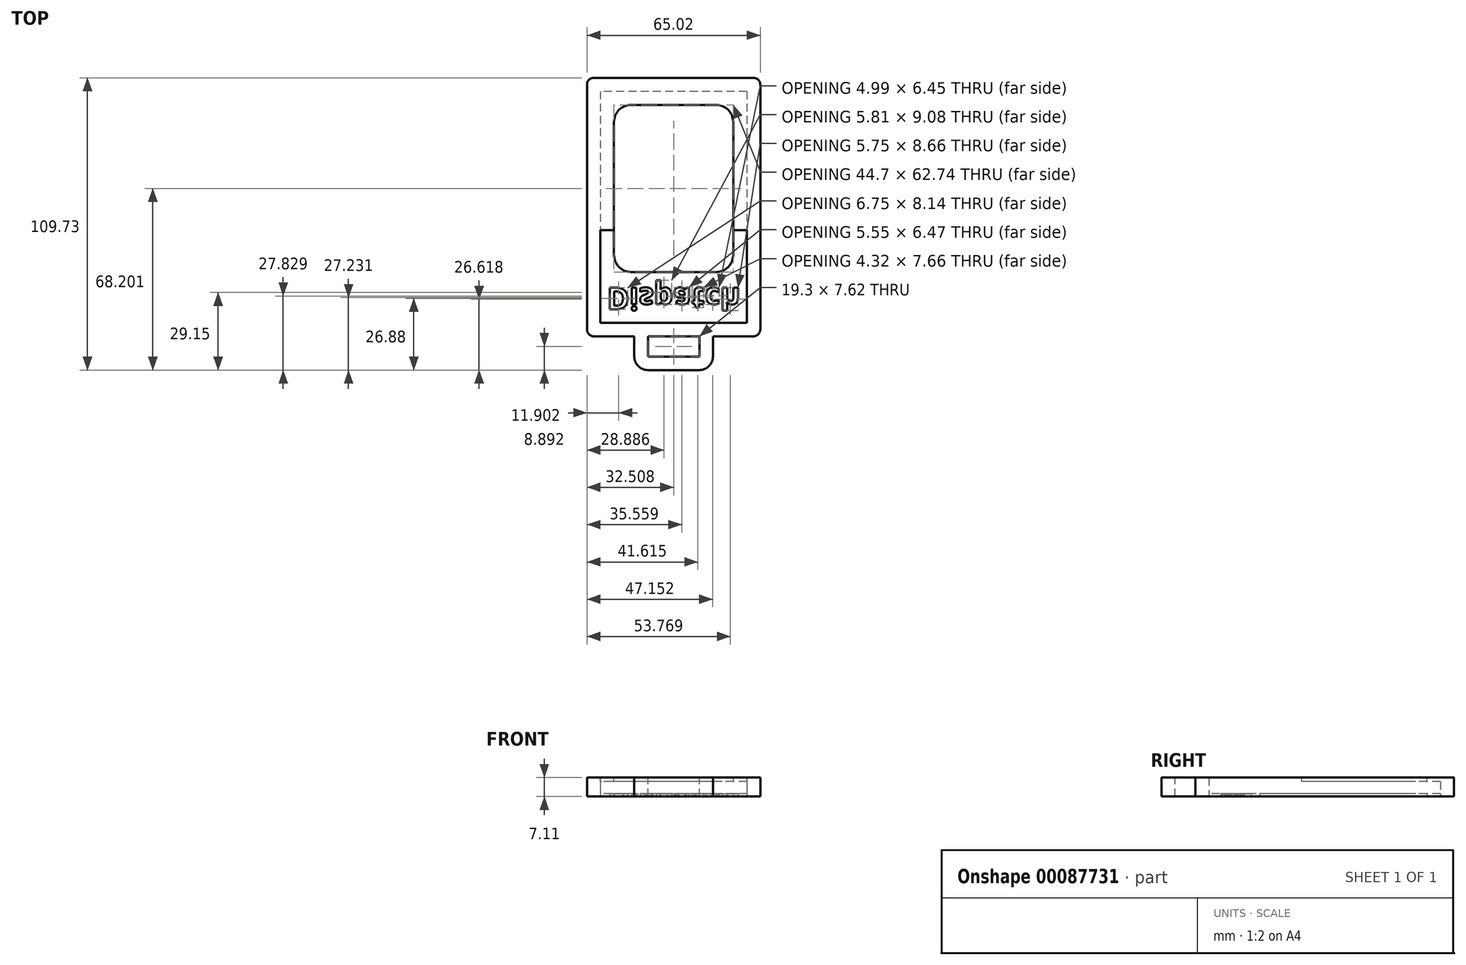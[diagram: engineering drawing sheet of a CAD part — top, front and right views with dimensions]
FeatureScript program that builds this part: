
annotation { "Feature Type Name" : "Feature", "Feature Type Description" : "" }
export const myFeature = defineFeature(function(context is Context, id is Id, definition is map)
    precondition{}
    {
        {
            var Q0;
            Q0=qCreatedBy(makeId("Top.planeOp"),FACE);
            var sketch = newSketch(context, id + "F0", { "sketchPlane" : qUnion([Q0])});
            skLineSegment(sketch, "E0.bottom", {"start": v(0, 0) * mm, "end": v(-54.86, 0) * mm});
            skLineSegment(sketch, "E0.top", {"start": v(0, -86.87) * mm, "end": v(-54.86, -86.87) * mm});
            skLineSegment(sketch, "E0.left", {"start": v(0, 0) * mm, "end": v(0, -86.87) * mm});
            skLineSegment(sketch, "E0.right", {"start": v(-54.86, 0) * mm, "end": v(-54.86, -86.87) * mm});
            skLineSegment(sketch, "E1.bottom", {"start": v(-59.94, 5.08) * mm, "end": v(5.08, 5.08) * mm});
            skLineSegment(sketch, "E1.top", {"start": v(-59.94, -91.95) * mm, "end": v(5.08, -91.95) * mm});
            skLineSegment(sketch, "E1.left", {"start": v(-59.94, 5.08) * mm, "end": v(-59.94, -91.95) * mm});
            skLineSegment(sketch, "E1.right", {"start": v(5.08, 5.08) * mm, "end": v(5.08, -91.95) * mm});
            skSolve(sketch);
        }
        {
            var Q0;
            Q0 = qSketchRegion(id + "F0", true);
            extrude(context, id + "F1", {"entities" : qUnion([Q0]), "depth" : 7.11 * mm});
        }
        {
            var Q0;
            Q0=makeQuery(id+"F1.opExtrude","CAP_FACE",FACE,{"disambiguationData":[OSD([sQuery(id+"F0.wireOp",EDGE,"E0.bottom"),sQuery(id+"F0.wireOp",EDGE,"E0.top"),sQuery(id+"F0.wireOp",EDGE,"E0.left"),sQuery(id+"F0.wireOp",EDGE,"E0.right"),sQuery(id+"F0.wireOp",EDGE,"E1.bottom"),sQuery(id+"F0.wireOp",EDGE,"E1.top"),sQuery(id+"F0.wireOp",EDGE,"E1.left"),sQuery(id+"F0.wireOp",EDGE,"E1.right")])],"isStart":true});
            var sketch = newSketch(context, id + "F2", { "sketchPlane" : qUnion([Q0])});
            skLineSegment(sketch, "E2.bottom", {"start": v(-54.86, 0) * mm, "end": v(0, 0) * mm});
            skLineSegment(sketch, "E2.top", {"start": v(-54.86, 86.87) * mm, "end": v(0, 86.87) * mm});
            skLineSegment(sketch, "E2.left", {"start": v(-54.86, 0) * mm, "end": v(-54.86, 86.87) * mm});
            skLineSegment(sketch, "E2.right", {"start": v(0, 0) * mm, "end": v(0, 86.87) * mm});
            skLineSegment(sketch, "E3.bottom", {"start": v(-43.43, 5.08) * mm, "end": v(-11.43, 5.08) * mm});
            skLineSegment(sketch, "E3.top", {"start": v(-43.43, 67.82) * mm, "end": v(-11.43, 67.82) * mm});
            skLineSegment(sketch, "E3.left", {"start": v(-49.78, 11.43) * mm, "end": v(-49.78, 61.47) * mm});
            skLineSegment(sketch, "E3.right", {"start": v(-5.08, 11.43) * mm, "end": v(-5.08, 61.47) * mm});
            skPoint(sketch, "E4.visualSharp", {"position": v(-49.78, 5.08) * mm});
            skArc(sketch, "E4.filletArc", {"start": v(-49.78, 11.43) * mm, "mid": v(-47.92, 6.94) * mm, "end": v(-43.43, 5.08) * mm});
            skPoint(sketch, "E5.visualSharp", {"position": v(-5.08, 5.08) * mm});
            skArc(sketch, "E5.filletArc", {"start": v(-11.43, 5.08) * mm, "mid": v(-6.94, 6.94) * mm, "end": v(-5.08, 11.43) * mm});
            skPoint(sketch, "E6.visualSharp", {"position": v(-5.08, 67.82) * mm});
            skArc(sketch, "E6.filletArc", {"start": v(-5.08, 61.47) * mm, "mid": v(-6.94, 65.96) * mm, "end": v(-11.43, 67.82) * mm});
            skPoint(sketch, "E7.visualSharp", {"position": v(-49.78, 67.82) * mm});
            skArc(sketch, "E7.filletArc", {"start": v(-43.43, 67.82) * mm, "mid": v(-47.92, 65.96) * mm, "end": v(-49.78, 61.47) * mm});
            skSolve(sketch);
        }
        {
            var Q0;
            Q0 = qSketchRegion(id + "F2", true);
            extrude(context, id + "F3", {"entities" : qUnion([Q0]), "oppositeDirection" : true, "depth" : 1.02 * mm});
        }
        {
            var Q0;
            Q0=makeQuery(id+"F3.opExtrude","CAP_FACE",FACE,{"disambiguationData":[OSD([sQuery(id+"F2.wireOp",EDGE,"E2.bottom"),sQuery(id+"F2.wireOp",EDGE,"E2.top"),sQuery(id+"F2.wireOp",EDGE,"E2.left"),sQuery(id+"F2.wireOp",EDGE,"E2.right"),sQuery(id+"F2.wireOp",EDGE,"E3.bottom"),sQuery(id+"F2.wireOp",EDGE,"E3.top"),sQuery(id+"F2.wireOp",EDGE,"E3.left"),sQuery(id+"F2.wireOp",EDGE,"E3.right"),sQuery(id+"F2.wireOp",EDGE,"E4.filletArc"),sQuery(id+"F2.wireOp",EDGE,"E5.filletArc"),sQuery(id+"F2.wireOp",EDGE,"E6.filletArc"),sQuery(id+"F2.wireOp",EDGE,"E7.filletArc")])],"isStart":true});
            var sketch = newSketch(context, id + "F4", { "sketchPlane" : qUnion([Q0])});
            skText(sketch, "E8", { "text": "Dispatch", "fontName": "OpenSans-Bold.ttf"});
            const initialGuessF4  = {"E8": [-0.05244, 0.0737, 1, 0, 0.00821]};
            skSetInitialGuess(sketch, initialGuessF4);
            skSolve(sketch);
        }
        {
            var Q0;
            Q0 = qSketchRegion(id + "F4", true);
            extrude(context, id + "F5", {"entities" : qUnion([Q0]), "operationType" : NewBodyOperationType.REMOVE, "oppositeDirection" : true, "depth" : 25.4 * mm});
        }
        {
            var Q0;
            Q0=makeQuery(id+"F1.opExtrude","CAP_FACE",FACE,{"disambiguationData":[OSD([sQuery(id+"F0.wireOp",EDGE,"E0.bottom"),sQuery(id+"F0.wireOp",EDGE,"E0.top"),sQuery(id+"F0.wireOp",EDGE,"E0.left"),sQuery(id+"F0.wireOp",EDGE,"E0.right"),sQuery(id+"F0.wireOp",EDGE,"E1.bottom"),sQuery(id+"F0.wireOp",EDGE,"E1.top"),sQuery(id+"F0.wireOp",EDGE,"E1.left"),sQuery(id+"F0.wireOp",EDGE,"E1.right")])],"isStart":false});
            var sketch = newSketch(context, id + "F6", { "sketchPlane" : qUnion([Q0])});
            skLineSegment(sketch, "E9.bottom", {"start": v(-42.16, -91.95) * mm, "end": v(-37.08, -91.95) * mm});
            skLineSegment(sketch, "E9.top", {"start": v(-37.08, -104.65) * mm, "end": v(-17.78, -104.65) * mm});
            skLineSegment(sketch, "E9.left", {"start": v(-42.16, -91.95) * mm, "end": v(-42.16, -99.57) * mm});
            skLineSegment(sketch, "E9.right", {"start": v(-12.7, -91.95) * mm, "end": v(-12.7, -99.57) * mm});
            skLineSegment(sketch, "E10.top", {"start": v(-37.08, -99.57) * mm, "end": v(-17.78, -99.57) * mm});
            skLineSegment(sketch, "E10.left", {"start": v(-37.08, -91.95) * mm, "end": v(-37.08, -99.57) * mm});
            skLineSegment(sketch, "E10.right", {"start": v(-17.78, -91.95) * mm, "end": v(-17.78, -99.57) * mm});
            skPoint(sketch, "E11.visualSharp", {"position": v(-12.7, -104.65) * mm});
            skArc(sketch, "E11.filletArc", {"start": v(-17.78, -104.65) * mm, "mid": v(-14.19, -103.16) * mm, "end": v(-12.7, -99.57) * mm});
            skPoint(sketch, "E12.visualSharp", {"position": v(-42.16, -104.65) * mm});
            skArc(sketch, "E12.filletArc", {"start": v(-42.16, -99.57) * mm, "mid": v(-40.68, -103.16) * mm, "end": v(-37.08, -104.65) * mm});
            skLineSegment(sketch, "E13.trimOffspring", {"start": v(-17.78, -91.95) * mm, "end": v(-12.7, -91.95) * mm});
            skSolve(sketch);
        }
        {
            var Q0;
            Q0 = qSketchRegion(id + "F6", true);
            var Q1;
            Q1=makeQuery(id+"F1.opExtrude","CAP_FACE",FACE,{"disambiguationData":[OSD([sQuery(id+"F0.wireOp",EDGE,"E0.bottom"),sQuery(id+"F0.wireOp",EDGE,"E0.top"),sQuery(id+"F0.wireOp",EDGE,"E0.left"),sQuery(id+"F0.wireOp",EDGE,"E0.right"),sQuery(id+"F0.wireOp",EDGE,"E1.bottom"),sQuery(id+"F0.wireOp",EDGE,"E1.top"),sQuery(id+"F0.wireOp",EDGE,"E1.left"),sQuery(id+"F0.wireOp",EDGE,"E1.right")])],"isStart":true});
            extrude(context, id + "F7", {"entities" : qUnion([Q0]), "operationType" : NewBodyOperationType.ADD, "endBound" : BoundingType.UP_TO_SURFACE, "oppositeDirection" : true, "endBoundEntityFace" : qUnion([Q1]), "depth" : 25.4 * mm});
        }
        {
            var Q0;
            Q0=makeQuery(id+"F7.boolean.opBoolean","MERGE",FACE,{"derivedFrom":[makeQuery(id+"F1.opExtrude","CAP_FACE",FACE,{"disambiguationData":[OSD([sQuery(id+"F0.wireOp",EDGE,"E0.bottom"),sQuery(id+"F0.wireOp",EDGE,"E0.top"),sQuery(id+"F0.wireOp",EDGE,"E0.left"),sQuery(id+"F0.wireOp",EDGE,"E0.right"),sQuery(id+"F0.wireOp",EDGE,"E1.bottom"),sQuery(id+"F0.wireOp",EDGE,"E1.top"),sQuery(id+"F0.wireOp",EDGE,"E1.left"),sQuery(id+"F0.wireOp",EDGE,"E1.right")])],"isStart":false}),makeQuery(id+"F7.opExtrude","CAP_FACE",FACE,{"disambiguationData":[OSD([sQuery(id+"F6.wireOp",EDGE,"E9.bottom"),sQuery(id+"F6.wireOp",EDGE,"E9.top"),sQuery(id+"F6.wireOp",EDGE,"E9.left"),sQuery(id+"F6.wireOp",EDGE,"E9.right"),sQuery(id+"F6.wireOp",EDGE,"E10.top"),sQuery(id+"F6.wireOp",EDGE,"E10.left"),sQuery(id+"F6.wireOp",EDGE,"E10.right"),sQuery(id+"F6.wireOp",EDGE,"E11.filletArc"),sQuery(id+"F6.wireOp",EDGE,"E12.filletArc"),sQuery(id+"F6.wireOp",EDGE,"E13.trimOffspring")])],"isStart":true})]});
            var sketch = newSketch(context, id + "F8", { "sketchPlane" : qUnion([Q0])});
            skLineSegment(sketch, "E14", {"start": v(0, 0) * mm, "end": v(0, -52.07) * mm});
            skLineSegment(sketch, "E15", {"start": v(0, -52.07) * mm, "end": v(-5.08, -52.07) * mm});
            skLineSegment(sketch, "E16", {"start": v(-5.08, -52.07) * mm, "end": v(-5.08, -11.43) * mm});
            skLineSegment(sketch, "E17", {"start": v(-11.43, -5.08) * mm, "end": v(-43.43, -5.08) * mm});
            skLineSegment(sketch, "E18", {"start": v(-49.78, -11.43) * mm, "end": v(-49.78, -52.07) * mm});
            skLineSegment(sketch, "E19", {"start": v(-49.78, -52.07) * mm, "end": v(-54.86, -52.07) * mm});
            skLineSegment(sketch, "E20", {"start": v(-54.86, -52.07) * mm, "end": v(-54.86, 0) * mm});
            skLineSegment(sketch, "E21", {"start": v(-54.86, 0) * mm, "end": v(0, 0) * mm});
            skPoint(sketch, "E22.visualSharp", {"position": v(-5.08, -5.08) * mm});
            skArc(sketch, "E22.filletArc", {"start": v(-5.08, -11.43) * mm, "mid": v(-6.94, -6.94) * mm, "end": v(-11.43, -5.08) * mm});
            skPoint(sketch, "E23.visualSharp", {"position": v(-49.78, -5.08) * mm});
            skArc(sketch, "E23.filletArc", {"start": v(-43.43, -5.08) * mm, "mid": v(-47.92, -6.94) * mm, "end": v(-49.78, -11.43) * mm});
            skSolve(sketch);
        }
        {
            var Q0;
            Q0 = qSketchRegion(id + "F8", true);
            extrude(context, id + "F9", {"entities" : qUnion([Q0]), "operationType" : NewBodyOperationType.ADD, "oppositeDirection" : true, "depth" : 1.52 * mm});
        }
        {
            var Q0;
            Q0=makeQuery(id+"F1.opExtrude","SWEPT_EDGE",EDGE,{"disambiguationData":[OSD([sQuery(id+"F0.wireOp",EDGE,"E1.top"),sQuery(id+"F0.wireOp",EDGE,"E1.left")])]});
            var Q1;
            Q1=makeQuery(id+"F1.opExtrude","SWEPT_EDGE",EDGE,{"disambiguationData":[OSD([sQuery(id+"F0.wireOp",EDGE,"E1.top"),sQuery(id+"F0.wireOp",EDGE,"E1.right")])]});
            var Q2;
            Q2=makeQuery(id+"F1.opExtrude","SWEPT_EDGE",EDGE,{"disambiguationData":[OSD([sQuery(id+"F0.wireOp",EDGE,"E1.bottom"),sQuery(id+"F0.wireOp",EDGE,"E1.left")])]});
            var Q3;
            Q3=makeQuery(id+"F1.opExtrude","SWEPT_EDGE",EDGE,{"disambiguationData":[OSD([sQuery(id+"F0.wireOp",EDGE,"E1.bottom"),sQuery(id+"F0.wireOp",EDGE,"E1.right")])]});
            fillet(context, id + "F10", {"entities" : qUnion([Q0, Q1, Q2, Q3]), "radius" : 2.54 * mm, "tangentPropagation" : true, "allowEdgeOverflow" : false});
        }
    });
